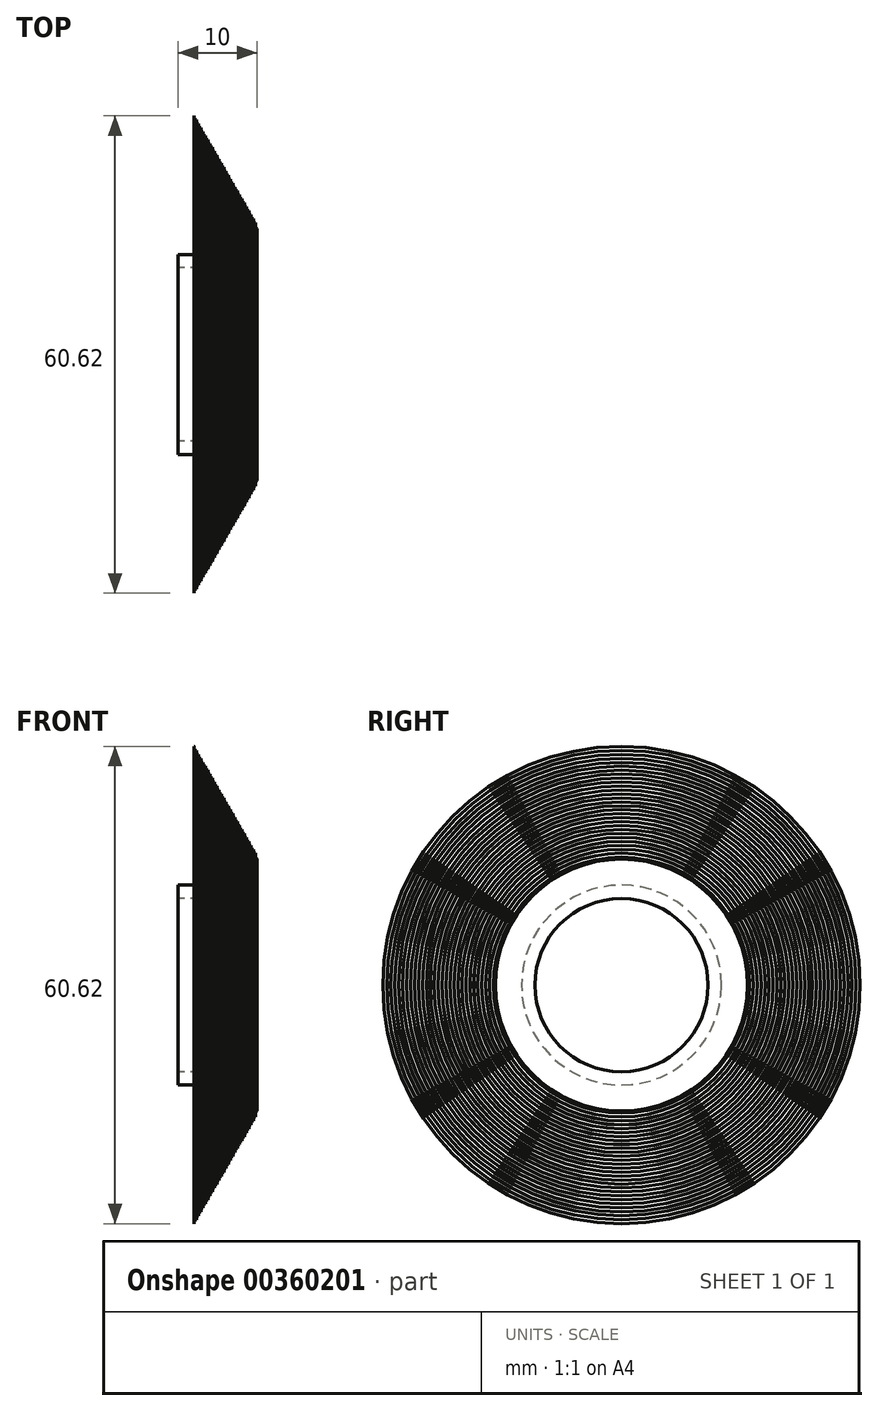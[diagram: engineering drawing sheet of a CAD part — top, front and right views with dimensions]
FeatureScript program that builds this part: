
annotation { "Feature Type Name" : "Feature", "Feature Type Description" : "" }
export const myFeature = defineFeature(function(context is Context, id is Id, definition is map)
    precondition{}
    {
        {
            var Q0;
            Q0=qCreatedBy(makeId("Right.planeOp"),FACE);
            var sketch = newSketch(context, id + "F0", { "sketchPlane" : qUnion([Q0])});
            skCircle(sketch, "E0", {"center": v(0, 0) * mm, "radius": 11.1 * mm});
            skCircle(sketch, "E1", {"center": v(0, 0) * mm, "radius": 12.7 * mm});
            skSolve(sketch);
        }
        {
            var Q0;
            Q0=qCreatedBy(makeId("Front.planeOp"),FACE);
            var sketch = newSketch(context, id + "F1", { "sketchPlane" : qUnion([Q0])});
            skLineSegment(sketch, "E2", {"start": v(0, 0) * mm, "end": v(0, 29.85) * mm, "construction": true});
            skLineSegment(sketch, "E3", {"start": v(0, 11) * mm, "end": v(0, 33.33) * mm});
            skLineSegment(sketch, "E4", {"start": v(0, 11) * mm, "end": v(10, 11) * mm});
            skLineSegment(sketch, "E5", {"start": v(10, 11) * mm, "end": v(10, 16) * mm});
            skLineSegment(sketch, "E6", {"start": v(10.02, 15.98) * mm, "end": v(0, 33.33) * mm, "construction": true});
            skLineSegment(sketch, "E7", {"start": v(0, 33.33) * mm, "end": v(0.29, 33.32) * mm});
            skLineSegment(sketch, "E8", {"start": v(0.29, 33.32) * mm, "end": v(0.29, 32.82) * mm});
            skLineSegment(sketch, "E9.1.0.0", {"start": v(0.29, 32.82) * mm, "end": v(0.58, 32.82) * mm});
            skLineSegment(sketch, "E9.1.0.1", {"start": v(0.58, 32.82) * mm, "end": v(0.58, 32.32) * mm});
            skLineSegment(sketch, "E9.2.0.0", {"start": v(0.58, 32.32) * mm, "end": v(0.87, 32.32) * mm});
            skLineSegment(sketch, "E9.2.0.1", {"start": v(0.87, 32.32) * mm, "end": v(0.87, 31.82) * mm});
            skLineSegment(sketch, "E9.3.0.0", {"start": v(0.87, 31.82) * mm, "end": v(1.16, 31.82) * mm});
            skLineSegment(sketch, "E9.3.0.1", {"start": v(1.16, 31.82) * mm, "end": v(1.16, 31.32) * mm});
            skLineSegment(sketch, "E9.4.0.0", {"start": v(1.16, 31.32) * mm, "end": v(1.45, 31.32) * mm});
            skLineSegment(sketch, "E9.4.0.1", {"start": v(1.45, 31.32) * mm, "end": v(1.45, 30.82) * mm});
            skLineSegment(sketch, "E9.5.0.0", {"start": v(1.45, 30.82) * mm, "end": v(1.74, 30.81) * mm});
            skLineSegment(sketch, "E9.5.0.1", {"start": v(1.74, 30.81) * mm, "end": v(1.74, 30.31) * mm});
            skLineSegment(sketch, "E9.6.0.0", {"start": v(1.74, 30.31) * mm, "end": v(2.03, 30.31) * mm});
            skLineSegment(sketch, "E9.6.0.1", {"start": v(2.03, 30.31) * mm, "end": v(2.03, 29.81) * mm});
            skLineSegment(sketch, "E9.7.0.0", {"start": v(2.03, 29.81) * mm, "end": v(2.32, 29.8) * mm});
            skLineSegment(sketch, "E9.7.0.1", {"start": v(2.32, 29.8) * mm, "end": v(2.32, 29.3) * mm});
            skLineSegment(sketch, "E9.8.0.0", {"start": v(2.32, 29.3) * mm, "end": v(2.6, 29.3) * mm});
            skLineSegment(sketch, "E9.8.0.1", {"start": v(2.6, 29.3) * mm, "end": v(2.6, 28.8) * mm});
            skLineSegment(sketch, "E9.9.0.0", {"start": v(2.6, 28.8) * mm, "end": v(2.9, 28.8) * mm});
            skLineSegment(sketch, "E9.9.0.1", {"start": v(2.9, 28.8) * mm, "end": v(2.9, 28.3) * mm});
            skLineSegment(sketch, "E9.10.0.0", {"start": v(2.9, 28.3) * mm, "end": v(3.19, 28.3) * mm});
            skLineSegment(sketch, "E9.10.0.1", {"start": v(3.19, 28.3) * mm, "end": v(3.19, 27.8) * mm});
            skLineSegment(sketch, "E9.11.0.0", {"start": v(3.19, 27.8) * mm, "end": v(3.48, 27.8) * mm});
            skLineSegment(sketch, "E9.11.0.1", {"start": v(3.48, 27.8) * mm, "end": v(3.48, 27.3) * mm});
            skLineSegment(sketch, "E9.12.0.0", {"start": v(3.48, 27.3) * mm, "end": v(3.77, 27.3) * mm});
            skLineSegment(sketch, "E9.12.0.1", {"start": v(3.77, 27.3) * mm, "end": v(3.77, 26.8) * mm});
            skLineSegment(sketch, "E9.13.0.0", {"start": v(3.77, 26.8) * mm, "end": v(4.06, 26.8) * mm});
            skLineSegment(sketch, "E9.13.0.1", {"start": v(4.06, 26.8) * mm, "end": v(4.06, 26.3) * mm});
            skLineSegment(sketch, "E9.14.0.0", {"start": v(4.06, 26.3) * mm, "end": v(4.35, 26.3) * mm});
            skLineSegment(sketch, "E9.14.0.1", {"start": v(4.35, 26.3) * mm, "end": v(4.35, 25.8) * mm});
            skLineSegment(sketch, "E9.direction1", {"start": v(0, 33.33) * mm, "end": v(0.14, 33.08) * mm, "construction": true});
            skLineSegment(sketch, "E10", {"start": v(0, 11) * mm, "end": v(0, 11) * mm});
            skLineSegment(sketch, "E11.0.15.0", {"start": v(4.35, 25.8) * mm, "end": v(4.64, 25.8) * mm});
            skLineSegment(sketch, "E11.3.15.0", {"start": v(4.64, 25.8) * mm, "end": v(4.64, 25.3) * mm});
            skLineSegment(sketch, "E12.0.16.0", {"start": v(4.64, 25.3) * mm, "end": v(4.93, 25.29) * mm});
            skLineSegment(sketch, "E12.3.16.0", {"start": v(4.93, 25.29) * mm, "end": v(4.93, 24.79) * mm});
            skLineSegment(sketch, "E13.0.17.0", {"start": v(4.93, 24.79) * mm, "end": v(5.22, 24.79) * mm});
            skLineSegment(sketch, "E13.3.17.0", {"start": v(5.22, 24.79) * mm, "end": v(5.22, 24.29) * mm});
            skLineSegment(sketch, "E14.0.18.0", {"start": v(5.22, 24.29) * mm, "end": v(5.5, 24.29) * mm});
            skLineSegment(sketch, "E14.3.18.0", {"start": v(5.5, 24.29) * mm, "end": v(5.5, 23.79) * mm});
            skLineSegment(sketch, "E15.0.19.0", {"start": v(5.5, 23.79) * mm, "end": v(5.8, 23.78) * mm});
            skLineSegment(sketch, "E15.3.19.0", {"start": v(5.8, 23.78) * mm, "end": v(5.8, 23.28) * mm});
            skLineSegment(sketch, "E16.0.20.0", {"start": v(5.8, 23.28) * mm, "end": v(6.09, 23.28) * mm});
            skLineSegment(sketch, "E16.3.20.0", {"start": v(6.09, 23.28) * mm, "end": v(6.09, 22.78) * mm});
            skLineSegment(sketch, "E17.0.21.0", {"start": v(6.09, 22.78) * mm, "end": v(6.38, 22.78) * mm});
            skLineSegment(sketch, "E17.3.21.0", {"start": v(6.38, 22.78) * mm, "end": v(6.38, 22.28) * mm});
            skLineSegment(sketch, "E18.0.22.0", {"start": v(6.38, 22.28) * mm, "end": v(6.67, 22.28) * mm});
            skLineSegment(sketch, "E18.3.22.0", {"start": v(6.67, 22.28) * mm, "end": v(6.67, 21.78) * mm});
            skLineSegment(sketch, "E19.0.23.0", {"start": v(6.67, 21.78) * mm, "end": v(6.96, 21.77) * mm});
            skLineSegment(sketch, "E19.3.23.0", {"start": v(6.96, 21.77) * mm, "end": v(6.96, 21.27) * mm});
            skLineSegment(sketch, "E20.0.24.0", {"start": v(6.96, 21.27) * mm, "end": v(7.25, 21.27) * mm});
            skLineSegment(sketch, "E20.3.24.0", {"start": v(7.25, 21.27) * mm, "end": v(7.25, 20.77) * mm});
            skLineSegment(sketch, "E21.0.25.0", {"start": v(7.25, 20.77) * mm, "end": v(7.54, 20.77) * mm});
            skLineSegment(sketch, "E21.3.25.0", {"start": v(7.54, 20.77) * mm, "end": v(7.54, 20.27) * mm});
            skLineSegment(sketch, "E22.0.26.0", {"start": v(7.54, 20.27) * mm, "end": v(7.83, 20.27) * mm});
            skLineSegment(sketch, "E22.3.26.0", {"start": v(7.83, 20.27) * mm, "end": v(7.83, 19.77) * mm});
            skLineSegment(sketch, "E23.0.27.0", {"start": v(7.83, 19.77) * mm, "end": v(8.12, 19.77) * mm});
            skLineSegment(sketch, "E23.3.27.0", {"start": v(8.12, 19.77) * mm, "end": v(8.12, 19.27) * mm});
            skLineSegment(sketch, "E24.0.28.0", {"start": v(8.12, 19.27) * mm, "end": v(8.4, 19.26) * mm});
            skLineSegment(sketch, "E24.3.28.0", {"start": v(8.4, 19.26) * mm, "end": v(8.4, 18.76) * mm});
            skLineSegment(sketch, "E25.0.29.0", {"start": v(8.4, 18.76) * mm, "end": v(8.7, 18.76) * mm});
            skLineSegment(sketch, "E25.3.29.0", {"start": v(8.7, 18.76) * mm, "end": v(8.7, 18.26) * mm});
            skLineSegment(sketch, "E26.0.30.0", {"start": v(8.7, 18.26) * mm, "end": v(8.99, 18.26) * mm});
            skLineSegment(sketch, "E26.3.30.0", {"start": v(8.99, 18.26) * mm, "end": v(8.99, 17.76) * mm});
            skLineSegment(sketch, "E27.0.31.0", {"start": v(8.99, 17.76) * mm, "end": v(9.28, 17.76) * mm});
            skLineSegment(sketch, "E27.3.31.0", {"start": v(9.28, 17.76) * mm, "end": v(9.28, 17.26) * mm});
            skLineSegment(sketch, "E28.0.32.0", {"start": v(9.28, 17.26) * mm, "end": v(9.57, 17.25) * mm});
            skLineSegment(sketch, "E28.3.32.0", {"start": v(9.57, 17.25) * mm, "end": v(9.57, 16.75) * mm});
            skLineSegment(sketch, "E29.0.33.0", {"start": v(9.57, 16.75) * mm, "end": v(9.86, 16.75) * mm});
            skLineSegment(sketch, "E29.3.33.0", {"start": v(9.86, 16.75) * mm, "end": v(9.86, 16.25) * mm});
            skLineSegment(sketch, "E30", {"start": v(9.86, 16.25) * mm, "end": v(10, 16) * mm});
            skLineSegment(sketch, "E31.bottom", {"start": v(10, 11) * mm, "end": v(7.5, 11) * mm});
            skLineSegment(sketch, "E31.top", {"start": v(10, 4.15) * mm, "end": v(7.5, 4.15) * mm});
            skLineSegment(sketch, "E31.left", {"start": v(10, 11) * mm, "end": v(10, 4.15) * mm});
            skLineSegment(sketch, "E31.right", {"start": v(7.5, 11) * mm, "end": v(7.5, 4.15) * mm});
            skSolve(sketch);
        }
        {
            var Q0;
            Q0=makeQuery(id+"F1.imprint","IMPRINT",FACE,{"disambiguationData":[TD([[makeQuery(id+"F1.imprint","IMPRINT",EDGE,{"derivedFrom":sQuery(id+"F1.wireOp",EDGE,"E3")}),-1.0]])]});
            var Q1;
            {var subQ0=sQuery(id+"F1.wireOp",EDGE,"E10");Q1=makeQuery(id+"F1.imprint","IMPRINT",FACE,{"disambiguationData":[TD([[makeQuery(id+"F1.imprint","IMPRINT",EDGE,{"derivedFrom":subQ0}),1.0]])]});}
            var Q2;
            Q2=makeQuery(id+"F1.imprint","IMPRINT",FACE,{"disambiguationData":[TD([[makeQuery(id+"F1.imprint","IMPRINT",EDGE,{"derivedFrom":sQuery(id+"F1.wireOp",EDGE,"E31.bottom")}),1.0]])]});
            var Q3;
            Q3=sQuery(id+"F0.wireOp",EDGE,"E1");
            revolve(context, id + "F2", {"entities" : qUnion([Q0, Q1, Q2]), "axis" : qUnion([Q3]), "revolveType" : RevolveType.FULL});
        }
        {
            var Q0;
            Q0=makeQuery(id+"F2.opRevolve","SWEPT_FACE",FACE,{"disambiguationData":[OSD([sQuery(id+"F1.wireOp",EDGE,"E3")])]});
            var sketch = newSketch(context, id + "F3", { "sketchPlane" : qUnion([Q0])});
            skPoint(sketch, "E32.0", {"position": v(0, 0) * mm});
            skCircle(sketch, "E33.0", {"center": v(0, 0) * mm, "radius": 12.7 * mm});
            skSolve(sketch);
        }
        {
            var Q0;
            Q0=makeQuery(id+"F3.imprint","IMPRINT",FACE,{"disambiguationData":[TD([[makeQuery(id+"F3.imprint","IMPRINT",EDGE,{"derivedFrom":sQuery(id+"F3.wireOp",EDGE,"E33.0")}),-1.0]])]});
            extrude(context, id + "F4", {"entities" : qUnion([Q0]), "operationType" : NewBodyOperationType.REMOVE, "oppositeDirection" : true, "depth" : 2 * mm});
        }
    });
